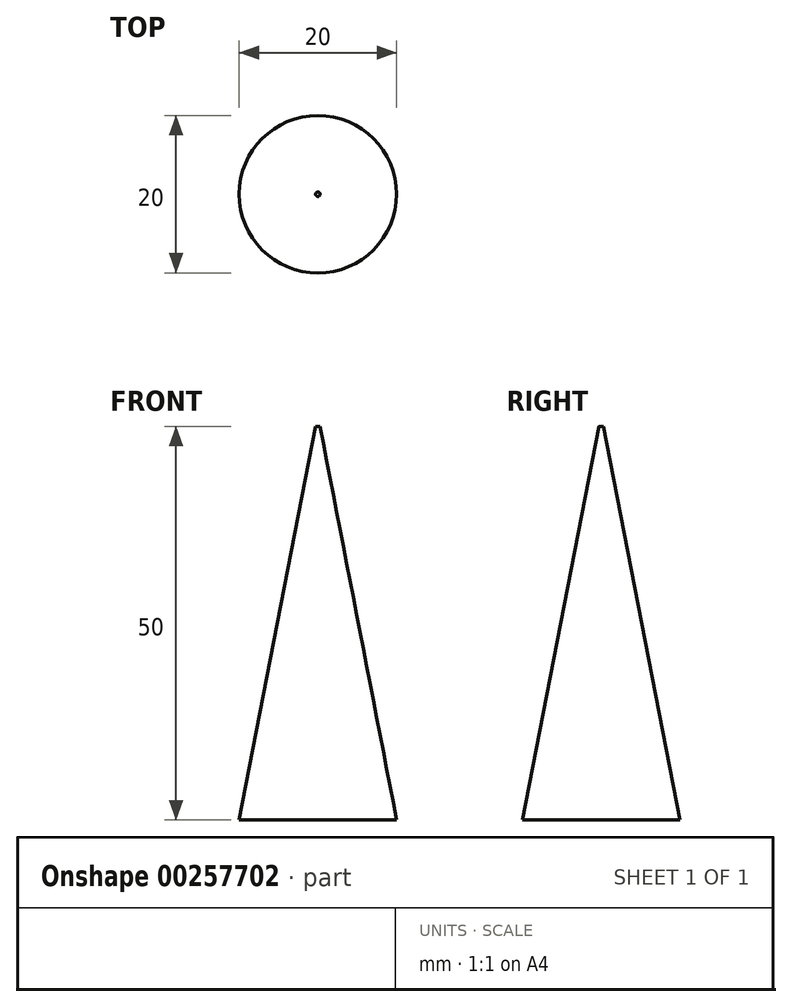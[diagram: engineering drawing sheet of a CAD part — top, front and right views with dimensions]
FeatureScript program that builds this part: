
annotation { "Feature Type Name" : "Feature", "Feature Type Description" : "" }
export const myFeature = defineFeature(function(context is Context, id is Id, definition is map)
    precondition{}
    {
        {
            var Q0;
            Q0=qCreatedBy(makeId("Top.planeOp"),FACE);
            var sketch = newSketch(context, id + "F0", { "sketchPlane" : qUnion([Q0])});
            skCircle(sketch, "E0", {"center": v(0, 0) * mm, "radius": 10 * mm});
            skSolve(sketch);
        }
        {
            var Q0;
            Q0=makeQuery(id+"F0.imprint","IMPRINT",FACE,{"disambiguationData":[TD([[makeQuery(id+"F0.imprint","IMPRINT",EDGE,{"derivedFrom":sQuery(id+"F0.wireOp",EDGE,"E0")}),1.0]])]});
            var Q1;
            Q1=sQuery(id+"F0.wireOp",EDGE,"E0");
            extrude(context, id + "F1", {"entities" : qUnion([Q0]), "surfaceEntities" : qUnion([Q1]), "depth" : 50 * mm, "hasDraft" : true, "draftAngle" : 11 * degree, "draftPullDirection" : true});
        }
    });
